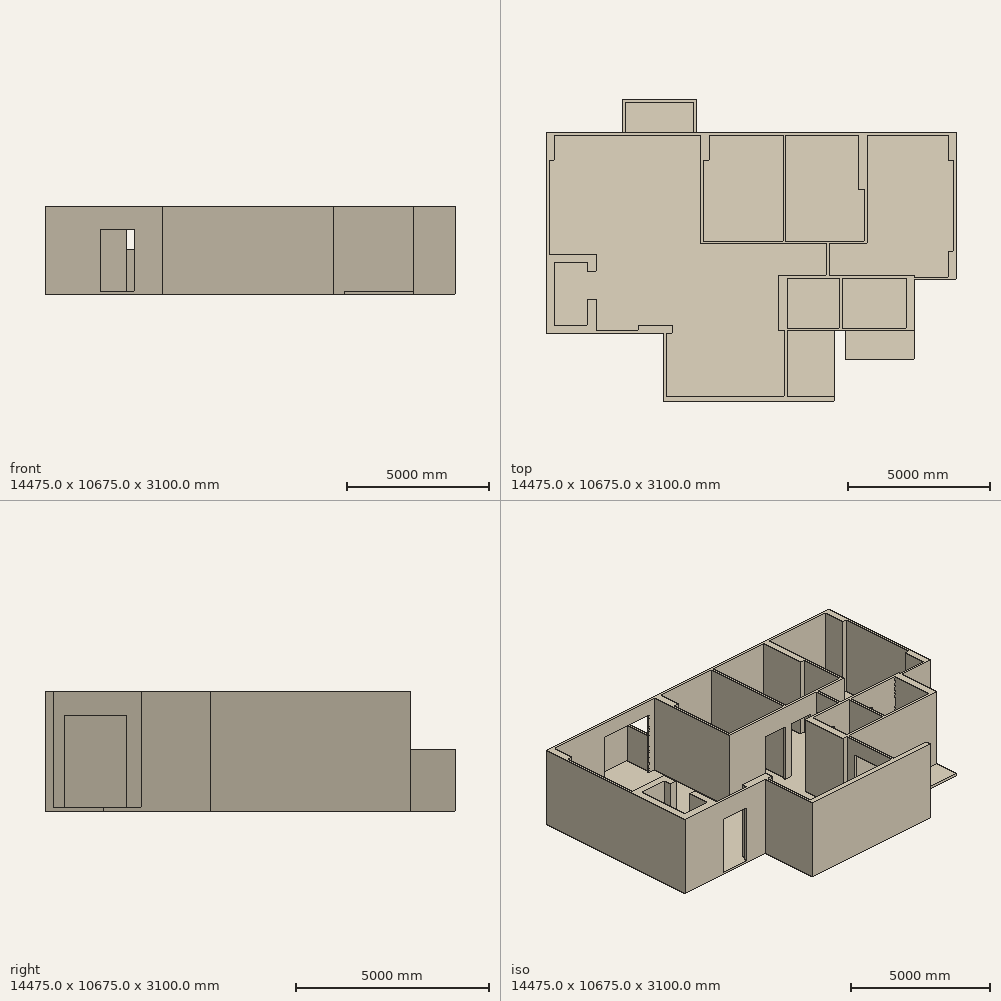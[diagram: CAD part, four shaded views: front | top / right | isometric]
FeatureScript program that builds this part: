
annotation { "Feature Type Name" : "Feature", "Feature Type Description" : "" }
export const myFeature = defineFeature(function(context is Context, id is Id, definition is map)
    precondition{}
    {
        {
            var Q0;
            Q0=qCreatedBy(makeId("Top.planeOp"),FACE);
            var sketch = newSketch(context, id + "F0", { "sketchPlane" : qUnion([Q0])});
            skLineSegment(sketch, "E0", {"start": v(0, 0) * mm, "end": v(-4125, 0) * mm});
            skLineSegment(sketch, "E1", {"start": v(-4125, 0) * mm, "end": v(-4125, 7100) * mm});
            skLineSegment(sketch, "E2", {"start": v(-4125, 7100) * mm, "end": v(-1425, 7100) * mm});
            skLineSegment(sketch, "E3", {"start": v(-1425, 7100) * mm, "end": v(-1425, 8275) * mm});
            skLineSegment(sketch, "E4", {"start": v(-1425, 8275) * mm, "end": v(1175, 8275) * mm});
            skLineSegment(sketch, "E5", {"start": v(1175, 8275) * mm, "end": v(1175, 7100) * mm});
            skLineSegment(sketch, "E6", {"start": v(1175, 7100) * mm, "end": v(10350, 7100) * mm});
            skLineSegment(sketch, "E7", {"start": v(10350, 7100) * mm, "end": v(10350, 1900) * mm});
            skLineSegment(sketch, "E8", {"start": v(10350, 1900) * mm, "end": v(8875, 1900) * mm});
            skLineSegment(sketch, "E9", {"start": v(8875, 1900) * mm, "end": v(8875, -900) * mm});
            skLineSegment(sketch, "E10", {"start": v(8875, -900) * mm, "end": v(6425, -900) * mm});
            skLineSegment(sketch, "E11", {"start": v(6050, -900) * mm, "end": v(6050, -2400) * mm});
            skLineSegment(sketch, "E12", {"start": v(6050, -2400) * mm, "end": v(0, -2400) * mm});
            skLineSegment(sketch, "E13", {"start": v(0, -2400) * mm, "end": v(0, 0) * mm});
            skLineSegment(sketch, "E14", {"start": v(6425, -900) * mm, "end": v(6425, 0) * mm});
            skLineSegment(sketch, "E15", {"start": v(6050, 0) * mm, "end": v(6050, -900) * mm});
            skLineSegment(sketch, "E16", {"start": v(6050, 0) * mm, "end": v(6050, 100) * mm});
            skLineSegment(sketch, "E17", {"start": v(6050, 100) * mm, "end": v(6425, 100) * mm});
            skLineSegment(sketch, "E18", {"start": v(6425, 100) * mm, "end": v(6425, 0) * mm});
            skSolve(sketch);
        }
        {
            var Q0;
            Q0=qSketchRegion(id+"F0",true);
            extrude(context, id + "F1", {"entities" : qUnion([Q0]), "oppositeDirection" : true, "depth" : 100 * mm});
        }
        {
            var Q0;
            Q0=makeQuery(id+"F1.opExtrude","CAP_FACE",FACE,{"disambiguationData":[OSD([sQuery(id+"F0.wireOp",EDGE,"E0"),sQuery(id+"F0.wireOp",EDGE,"E1"),sQuery(id+"F0.wireOp",EDGE,"E2"),sQuery(id+"F0.wireOp",EDGE,"E3"),sQuery(id+"F0.wireOp",EDGE,"E4"),sQuery(id+"F0.wireOp",EDGE,"E5"),sQuery(id+"F0.wireOp",EDGE,"E6"),sQuery(id+"F0.wireOp",EDGE,"E7"),sQuery(id+"F0.wireOp",EDGE,"E8"),sQuery(id+"F0.wireOp",EDGE,"E9"),sQuery(id+"F0.wireOp",EDGE,"E10"),sQuery(id+"F0.wireOp",EDGE,"E11"),sQuery(id+"F0.wireOp",EDGE,"E12"),sQuery(id+"F0.wireOp",EDGE,"E13"),sQuery(id+"F0.wireOp",EDGE,"E14"),sQuery(id+"F0.wireOp",EDGE,"EO6Hl1aY-iN83-L0no-XnAw-wlp1sX6jhs91"),sQuery(id+"F0.wireOp",EDGE,"E15")])],"isStart":true});
            var sketch = newSketch(context, id + "F2", { "sketchPlane" : qUnion([Q0])});
            skLineSegment(sketch, "E19", {"start": v(-4125, 0) * mm, "end": v(-4125, 2800) * mm});
            skLineSegment(sketch, "E20", {"start": v(-4125, 2800) * mm, "end": v(-2375, 2800) * mm});
            skLineSegment(sketch, "E21", {"start": v(-2375, 2800) * mm, "end": v(-2375, 2200) * mm});
            skLineSegment(sketch, "E22", {"start": v(-2375, 2200) * mm, "end": v(-2675, 2200) * mm});
            skLineSegment(sketch, "E23", {"start": v(-2675, 2200) * mm, "end": v(-2675, 2500) * mm});
            skLineSegment(sketch, "E24", {"start": v(-2675, 2500) * mm, "end": v(-3825, 2500) * mm});
            skLineSegment(sketch, "E25", {"start": v(-3825, 2500) * mm, "end": v(-3825, 300) * mm});
            skLineSegment(sketch, "E26", {"start": v(-3825, 300) * mm, "end": v(-2675, 300) * mm});
            skLineSegment(sketch, "E27", {"start": v(-2675, 300) * mm, "end": v(-2675, 1200) * mm});
            skLineSegment(sketch, "E28", {"start": v(-2675, 1200) * mm, "end": v(-2375, 1200) * mm});
            skLineSegment(sketch, "E29", {"start": v(-2375, 1200) * mm, "end": v(-2375, 0) * mm});
            skLineSegment(sketch, "E30", {"start": v(-2375, 0) * mm, "end": v(-4125, 0) * mm});
            skSolve(sketch);
        }
        {
            var Q0;
            Q0=qSketchRegion(id+"F2",true);
            extrude(context, id + "F3", {"entities" : qUnion([Q0]), "operationType" : NewBodyOperationType.ADD, "depth" : 3000 * mm});
        }
        {
            var Q0;
            Q0=makeQuery(id+"F1.opExtrude","CAP_FACE",FACE,{"disambiguationData":[OSD([sQuery(id+"F0.wireOp",EDGE,"E0"),sQuery(id+"F0.wireOp",EDGE,"E1"),sQuery(id+"F0.wireOp",EDGE,"E2"),sQuery(id+"F0.wireOp",EDGE,"E3"),sQuery(id+"F0.wireOp",EDGE,"E4"),sQuery(id+"F0.wireOp",EDGE,"E5"),sQuery(id+"F0.wireOp",EDGE,"E6"),sQuery(id+"F0.wireOp",EDGE,"E7"),sQuery(id+"F0.wireOp",EDGE,"E8"),sQuery(id+"F0.wireOp",EDGE,"E9"),sQuery(id+"F0.wireOp",EDGE,"E10"),sQuery(id+"F0.wireOp",EDGE,"E11"),sQuery(id+"F0.wireOp",EDGE,"E12"),sQuery(id+"F0.wireOp",EDGE,"E13"),sQuery(id+"F0.wireOp",EDGE,"E14"),sQuery(id+"F0.wireOp",EDGE,"EO6Hl1aY-iN83-L0no-XnAw-wlp1sX6jhs91"),sQuery(id+"F0.wireOp",EDGE,"E15")])],"isStart":true});
            var sketch = newSketch(context, id + "F4", { "sketchPlane" : qUnion([Q0])});
            skLineSegment(sketch, "E31.bottom", {"start": v(-4125, 7100) * mm, "end": v(-3825, 7100) * mm});
            skLineSegment(sketch, "E31.top", {"start": v(-4125, 6100) * mm, "end": v(-3825, 6100) * mm});
            skLineSegment(sketch, "E31.left", {"start": v(-4125, 7100) * mm, "end": v(-4125, 6100) * mm});
            skLineSegment(sketch, "E31.right", {"start": v(-3825, 7100) * mm, "end": v(-3825, 6100) * mm});
            skLineSegment(sketch, "E32.bottom", {"start": v(1325, 7100) * mm, "end": v(1625, 7100) * mm});
            skLineSegment(sketch, "E32.top", {"start": v(1325, 6100) * mm, "end": v(1625, 6100) * mm});
            skLineSegment(sketch, "E32.left", {"start": v(1325, 7100) * mm, "end": v(1325, 6100) * mm});
            skLineSegment(sketch, "E32.right", {"start": v(1625, 7100) * mm, "end": v(1625, 6100) * mm});
            skLineSegment(sketch, "E33.bottom", {"start": v(6900, 7100) * mm, "end": v(7200, 7100) * mm});
            skLineSegment(sketch, "E33.top", {"start": v(6900, 5100) * mm, "end": v(7200, 5100) * mm});
            skLineSegment(sketch, "E33.left", {"start": v(6900, 7100) * mm, "end": v(6900, 5100) * mm});
            skLineSegment(sketch, "E33.right", {"start": v(7200, 7100) * mm, "end": v(7200, 5100) * mm});
            skLineSegment(sketch, "E34.bottom", {"start": v(10350, 7100) * mm, "end": v(10050, 7100) * mm});
            skLineSegment(sketch, "E34.top", {"start": v(10350, 6100) * mm, "end": v(10050, 6100) * mm});
            skLineSegment(sketch, "E34.left", {"start": v(10350, 7100) * mm, "end": v(10350, 6100) * mm});
            skLineSegment(sketch, "E34.right", {"start": v(10050, 7100) * mm, "end": v(10050, 6100) * mm});
            skLineSegment(sketch, "E35.bottom", {"start": v(10350, 1900) * mm, "end": v(10050, 1900) * mm});
            skLineSegment(sketch, "E35.top", {"start": v(10350, 2900) * mm, "end": v(10050, 2900) * mm});
            skLineSegment(sketch, "E35.left", {"start": v(10350, 1900) * mm, "end": v(10350, 2900) * mm});
            skLineSegment(sketch, "E35.right", {"start": v(10050, 1900) * mm, "end": v(10050, 2900) * mm});
            skLineSegment(sketch, "E36.bottom", {"start": v(8875, 2050) * mm, "end": v(8575, 2050) * mm});
            skLineSegment(sketch, "E36.top", {"start": v(8875, 100) * mm, "end": v(8575, 100) * mm});
            skLineSegment(sketch, "E36.left", {"start": v(8875, 2050) * mm, "end": v(8875, 100) * mm});
            skLineSegment(sketch, "E36.right", {"start": v(8575, 2050) * mm, "end": v(8575, 100) * mm});
            skLineSegment(sketch, "E37.bottom", {"start": v(4375, 2050) * mm, "end": v(4075, 2050) * mm});
            skLineSegment(sketch, "E37.top", {"start": v(4375, 100) * mm, "end": v(4075, 100) * mm});
            skLineSegment(sketch, "E37.left", {"start": v(4375, 2050) * mm, "end": v(4375, 100) * mm});
            skLineSegment(sketch, "E37.right", {"start": v(4075, 2050) * mm, "end": v(4075, 100) * mm});
            skLineSegment(sketch, "E38.bottom", {"start": v(325, 0) * mm, "end": v(-875, 0) * mm});
            skLineSegment(sketch, "E38.top", {"start": v(325, 300) * mm, "end": v(-875, 300) * mm});
            skLineSegment(sketch, "E38.left", {"start": v(325, 0) * mm, "end": v(325, 300) * mm});
            skLineSegment(sketch, "E38.right", {"start": v(-875, 0) * mm, "end": v(-875, 300) * mm});
            skLineSegment(sketch, "E39.bottom", {"start": v(0, -2400) * mm, "end": v(6050, -2400) * mm});
            skLineSegment(sketch, "E39.top", {"start": v(0, -2200) * mm, "end": v(6050, -2200) * mm});
            skLineSegment(sketch, "E39.left", {"start": v(0, -2400) * mm, "end": v(0, -2200) * mm});
            skLineSegment(sketch, "E39.right", {"start": v(6050, -2400) * mm, "end": v(6050, -2200) * mm});
            skSolve(sketch);
        }
        {
            var Q0;
            Q0=qSketchRegion(id+"F4",true);
            extrude(context, id + "F5", {"entities" : qUnion([Q0]), "operationType" : NewBodyOperationType.ADD, "depth" : 3000 * mm});
        }
        {
            var Q0;
            Q0=makeQuery(id+"F1.opExtrude","CAP_FACE",FACE,{"disambiguationData":[OSD([sQuery(id+"F0.wireOp",EDGE,"E0"),sQuery(id+"F0.wireOp",EDGE,"E1"),sQuery(id+"F0.wireOp",EDGE,"E2"),sQuery(id+"F0.wireOp",EDGE,"E3"),sQuery(id+"F0.wireOp",EDGE,"E4"),sQuery(id+"F0.wireOp",EDGE,"E5"),sQuery(id+"F0.wireOp",EDGE,"E6"),sQuery(id+"F0.wireOp",EDGE,"E7"),sQuery(id+"F0.wireOp",EDGE,"E8"),sQuery(id+"F0.wireOp",EDGE,"E9"),sQuery(id+"F0.wireOp",EDGE,"E10"),sQuery(id+"F0.wireOp",EDGE,"E11"),sQuery(id+"F0.wireOp",EDGE,"E12"),sQuery(id+"F0.wireOp",EDGE,"E13"),sQuery(id+"F0.wireOp",EDGE,"E14"),sQuery(id+"F0.wireOp",EDGE,"EO6Hl1aY-iN83-L0no-XnAw-wlp1sX6jhs91"),sQuery(id+"F0.wireOp",EDGE,"E15")])],"isStart":true});
            var sketch = newSketch(context, id + "F6", { "sketchPlane" : qUnion([Q0])});
            skLineSegment(sketch, "E40", {"start": v(0, -2200) * mm, "end": v(0, 0) * mm});
            skLineSegment(sketch, "E41", {"start": v(0, 0) * mm, "end": v(-4125, 0) * mm});
            skLineSegment(sketch, "E42", {"start": v(-4125, 0) * mm, "end": v(-4125, 7100) * mm});
            skLineSegment(sketch, "E43", {"start": v(-4125, 7100) * mm, "end": v(-1425, 7100) * mm});
            skLineSegment(sketch, "E44", {"start": v(-1425, 7100) * mm, "end": v(-1425, 7000) * mm});
            skLineSegment(sketch, "E45", {"start": v(-1425, 7000) * mm, "end": v(-4025, 7000) * mm});
            skLineSegment(sketch, "E46", {"start": v(-4025, 7000) * mm, "end": v(-4025, 100) * mm});
            skLineSegment(sketch, "E47", {"start": v(-4025, 100) * mm, "end": v(100, 100) * mm});
            skLineSegment(sketch, "E48", {"start": v(100, 100) * mm, "end": v(100, -2200) * mm});
            skLineSegment(sketch, "E49", {"start": v(100, -2200) * mm, "end": v(0, -2200) * mm});
            skLineSegment(sketch, "E50.bottom", {"start": v(-1425, 7100) * mm, "end": v(1325, 7100) * mm});
            skLineSegment(sketch, "E50.top", {"start": v(-1425, 7000) * mm, "end": v(1325, 7000) * mm});
            skLineSegment(sketch, "E50.right", {"start": v(1325, 7100) * mm, "end": v(1325, 7000) * mm});
            skSolve(sketch);
        }
        {
            var Q0;
            Q0=qSketchRegion(id+"F6",true);
            extrude(context, id + "F7", {"entities" : qUnion([Q0]), "depth" : 3000 * mm});
        }
        {
            var Q0;
            Q0=makeQuery(id+"F1.opExtrude","CAP_FACE",FACE,{"disambiguationData":[OSD([sQuery(id+"F0.wireOp",EDGE,"E0"),sQuery(id+"F0.wireOp",EDGE,"E1"),sQuery(id+"F0.wireOp",EDGE,"E2"),sQuery(id+"F0.wireOp",EDGE,"E3"),sQuery(id+"F0.wireOp",EDGE,"E4"),sQuery(id+"F0.wireOp",EDGE,"E5"),sQuery(id+"F0.wireOp",EDGE,"E6"),sQuery(id+"F0.wireOp",EDGE,"E7"),sQuery(id+"F0.wireOp",EDGE,"E8"),sQuery(id+"F0.wireOp",EDGE,"E9"),sQuery(id+"F0.wireOp",EDGE,"E10"),sQuery(id+"F0.wireOp",EDGE,"E11"),sQuery(id+"F0.wireOp",EDGE,"E12"),sQuery(id+"F0.wireOp",EDGE,"E13"),sQuery(id+"F0.wireOp",EDGE,"E14"),sQuery(id+"F0.wireOp",EDGE,"EO6Hl1aY-iN83-L0no-XnAw-wlp1sX6jhs91"),sQuery(id+"F0.wireOp",EDGE,"E15")])],"isStart":true});
            var sketch = newSketch(context, id + "F8", { "sketchPlane" : qUnion([Q0])});
            skLineSegment(sketch, "E51", {"start": v(7200, 3170) * mm, "end": v(7200, 7100) * mm});
            skLineSegment(sketch, "E52", {"start": v(7200, 7100) * mm, "end": v(1325, 7100) * mm});
            skLineSegment(sketch, "E53", {"start": v(1325, 7100) * mm, "end": v(1325, 3170) * mm});
            skLineSegment(sketch, "E54", {"start": v(1325, 3170) * mm, "end": v(5775, 3170) * mm});
            skLineSegment(sketch, "E55.bottom", {"start": v(1425, 3270) * mm, "end": v(4225, 3270) * mm});
            skLineSegment(sketch, "E55.top", {"start": v(1425, 7000) * mm, "end": v(4225, 7000) * mm});
            skLineSegment(sketch, "E55.left", {"start": v(1425, 3270) * mm, "end": v(1425, 7000) * mm});
            skLineSegment(sketch, "E55.right", {"start": v(4225, 3270) * mm, "end": v(4225, 7000) * mm});
            skLineSegment(sketch, "E56.bottom", {"start": v(4325, 7000) * mm, "end": v(7100, 7000) * mm});
            skLineSegment(sketch, "E56.top", {"start": v(4325, 3270) * mm, "end": v(7100, 3270) * mm});
            skLineSegment(sketch, "E56.left", {"start": v(4325, 7000) * mm, "end": v(4325, 3270) * mm});
            skLineSegment(sketch, "E56.right", {"start": v(7100, 7000) * mm, "end": v(7100, 3270) * mm});
            skLineSegment(sketch, "E57.bottom", {"start": v(7200, 7100) * mm, "end": v(10350, 7100) * mm});
            skLineSegment(sketch, "E57.top", {"start": v(7200, 7000) * mm, "end": v(10250, 7000) * mm});
            skLineSegment(sketch, "E57.left", {"start": v(7200, 7100) * mm, "end": v(7200, 7000) * mm});
            skLineSegment(sketch, "E57.right", {"start": v(10350, 7100) * mm, "end": v(10350, 7000) * mm});
            skLineSegment(sketch, "E58.bottom", {"start": v(10350, 7100) * mm, "end": v(10250, 7100) * mm});
            skLineSegment(sketch, "E58.top", {"start": v(10350, 1900) * mm, "end": v(10250, 1900) * mm});
            skLineSegment(sketch, "E58.left", {"start": v(10350, 7100) * mm, "end": v(10350, 1900) * mm});
            skLineSegment(sketch, "E58.right", {"start": v(10250, 7000) * mm, "end": v(10250, 1975) * mm});
            skPoint(sketch, "E59.oppositeSnap0", {"position": v(8875, 1975) * mm});
            skLineSegment(sketch, "E59.bottom", {"start": v(10250, 1900) * mm, "end": v(8875, 1900) * mm});
            skLineSegment(sketch, "E59.top", {"start": v(10250, 1975) * mm, "end": v(8875, 1975) * mm});
            skLineSegment(sketch, "E59.right", {"start": v(8875, 1900) * mm, "end": v(8875, 1975) * mm});
            skLineSegment(sketch, "E60.bottom", {"start": v(8575, 2050) * mm, "end": v(5875, 2050) * mm});
            skLineSegment(sketch, "E60.top", {"start": v(8575, 1950) * mm, "end": v(6325, 1950) * mm});
            skLineSegment(sketch, "E60.left", {"start": v(8575, 2050) * mm, "end": v(8575, 1950) * mm});
            skLineSegment(sketch, "E60.right", {"start": v(4375, 2050) * mm, "end": v(4375, 1950) * mm});
            skLineSegment(sketch, "E61.bottom", {"start": v(4375, 100) * mm, "end": v(8575, 100) * mm});
            skLineSegment(sketch, "E61.top", {"start": v(4375, 200) * mm, "end": v(6225, 200) * mm});
            skLineSegment(sketch, "E61.left", {"start": v(4375, 100) * mm, "end": v(4375, 200) * mm});
            skLineSegment(sketch, "E61.right", {"start": v(8575, 100) * mm, "end": v(8575, 200) * mm});
            skLineSegment(sketch, "E62.left", {"start": v(6225, 1950) * mm, "end": v(6225, 200) * mm});
            skLineSegment(sketch, "E62.right", {"start": v(6325, 1950) * mm, "end": v(6325, 200) * mm});
            skLineSegment(sketch, "E63.trimOffspring", {"start": v(6225, 1950) * mm, "end": v(4375, 1950) * mm});
            skLineSegment(sketch, "E64.trimOffspring", {"start": v(6325, 200) * mm, "end": v(8575, 200) * mm});
            skLineSegment(sketch, "E65.left", {"start": v(5775, 3170) * mm, "end": v(5775, 2050) * mm});
            skLineSegment(sketch, "E65.right", {"start": v(5875, 3170) * mm, "end": v(5875, 2050) * mm});
            skLineSegment(sketch, "E66.trimOffspring", {"start": v(5875, 3170) * mm, "end": v(7200, 3170) * mm});
            skLineSegment(sketch, "E67.trimOffspring", {"start": v(5775, 2050) * mm, "end": v(4375, 2050) * mm});
            skLineSegment(sketch, "E68.bottom", {"start": v(4375, 200) * mm, "end": v(4275, 200) * mm});
            skLineSegment(sketch, "E68.top", {"start": v(4375, -2400) * mm, "end": v(4275, -2400) * mm});
            skLineSegment(sketch, "E68.left", {"start": v(4375, 200) * mm, "end": v(4375, -2400) * mm});
            skLineSegment(sketch, "E68.right", {"start": v(4275, 200) * mm, "end": v(4275, -2400) * mm});
            skSolve(sketch);
        }
        {
            var Q0;
            Q0=qSketchRegion(id+"F8",true);
            extrude(context, id + "F9", {"entities" : qUnion([Q0]), "operationType" : NewBodyOperationType.ADD, "depth" : 3000 * mm});
        }
        {
            var Q0;
            Q0=makeQuery(id+"F7.opExtrude","SWEPT_FACE",FACE,{"disambiguationData":[OSD([sQuery(id+"F6.wireOp",EDGE,"E41")])]});
            var sketch = newSketch(context, id + "F10", { "sketchPlane" : qUnion([Q0])});
            skLineSegment(sketch, "E69.bottom", {"start": v(-975, 0) * mm, "end": v(-2175, 0) * mm});
            skLineSegment(sketch, "E69.top", {"start": v(-975, 2200) * mm, "end": v(-2175, 2200) * mm});
            skLineSegment(sketch, "E69.left", {"start": v(-975, 0) * mm, "end": v(-975, 2200) * mm});
            skLineSegment(sketch, "E69.right", {"start": v(-2175, 0) * mm, "end": v(-2175, 2200) * mm});
            skSolve(sketch);
        }
        {
            var Q0;
            Q0=qSketchRegion(id+"F10",true);
            extrude(context, id + "F11", {"entities" : qUnion([Q0]), "operationType" : NewBodyOperationType.REMOVE, "oppositeDirection" : true, "depth" : 100 * mm});
        }
        {
            var Q0;
            Q0=makeQuery(id+"F9.opExtrude","SWEPT_FACE",FACE,{"disambiguationData":[OSD([sQuery(id+"F8.wireOp",EDGE,"E54")])]});
            var sketch = newSketch(context, id + "F12", { "sketchPlane" : qUnion([Q0])});
            skLineSegment(sketch, "E70.bottom", {"start": v(3175, 2200) * mm, "end": v(4175, 2200) * mm});
            skLineSegment(sketch, "E70.top", {"start": v(3175, 0) * mm, "end": v(4175, 0) * mm});
            skLineSegment(sketch, "E70.left", {"start": v(3175, 2200) * mm, "end": v(3175, 0) * mm});
            skLineSegment(sketch, "E70.right", {"start": v(4175, 2200) * mm, "end": v(4175, 0) * mm});
            skLineSegment(sketch, "E71.bottom", {"start": v(4475, 2200) * mm, "end": v(5475, 2200) * mm});
            skLineSegment(sketch, "E71.top", {"start": v(4475, 0) * mm, "end": v(5475, 0) * mm});
            skLineSegment(sketch, "E71.left", {"start": v(4475, 2200) * mm, "end": v(4475, 0) * mm});
            skLineSegment(sketch, "E71.right", {"start": v(5475, 2200) * mm, "end": v(5475, 0) * mm});
            skSolve(sketch);
        }
        {
            var Q0;
            Q0=qSketchRegion(id+"F12",true);
            extrude(context, id + "F13", {"entities" : qUnion([Q0]), "operationType" : NewBodyOperationType.REMOVE, "oppositeDirection" : true, "depth" : 100 * mm});
        }
        {
            var Q0;
            Q0=makeQuery(id+"F9.opExtrude","SWEPT_FACE",FACE,{"disambiguationData":[OSD([sQuery(id+"F8.wireOp",EDGE,"E65.left")])]});
            var sketch = newSketch(context, id + "F14", { "sketchPlane" : qUnion([Q0])});
            skLineSegment(sketch, "E72.bottom", {"start": v(-3110, 2200) * mm, "end": v(-2110, 2200) * mm});
            skLineSegment(sketch, "E72.top", {"start": v(-3110, 0) * mm, "end": v(-2110, 0) * mm});
            skLineSegment(sketch, "E72.left", {"start": v(-3110, 2200) * mm, "end": v(-3110, 0) * mm});
            skLineSegment(sketch, "E72.right", {"start": v(-2110, 2200) * mm, "end": v(-2110, 0) * mm});
            skSolve(sketch);
        }
        {
            var Q0;
            Q0=qSketchRegion(id+"F14",true);
            extrude(context, id + "F15", {"entities" : qUnion([Q0]), "operationType" : NewBodyOperationType.REMOVE, "oppositeDirection" : true, "depth" : 100 * mm});
        }
        {
            var Q0;
            Q0=makeQuery(id+"F9.opExtrude","SWEPT_FACE",FACE,{"disambiguationData":[OSD([sQuery(id+"F8.wireOp",EDGE,"E67.trimOffspring")])]});
            var sketch = newSketch(context, id + "F16", { "sketchPlane" : qUnion([Q0])});
            skLineSegment(sketch, "E73.bottom", {"start": v(-5475, 2200) * mm, "end": v(-4475, 2200) * mm});
            skLineSegment(sketch, "E73.top", {"start": v(-5475, 0) * mm, "end": v(-4475, 0) * mm});
            skLineSegment(sketch, "E73.left", {"start": v(-5475, 2200) * mm, "end": v(-5475, 0) * mm});
            skLineSegment(sketch, "E73.right", {"start": v(-4475, 2200) * mm, "end": v(-4475, 0) * mm});
            skPoint(sketch, "E74.oppositeSnap0", {"position": v(-5075, 0) * mm});
            skLineSegment(sketch, "E74.bottom", {"start": v(-6425, 2200) * mm, "end": v(-7425, 2200) * mm});
            skLineSegment(sketch, "E74.top", {"start": v(-6425, 0) * mm, "end": v(-7425, 0) * mm});
            skLineSegment(sketch, "E74.left", {"start": v(-6425, 2200) * mm, "end": v(-6425, 0) * mm});
            skLineSegment(sketch, "E74.right", {"start": v(-7425, 2200) * mm, "end": v(-7425, 0) * mm});
            skSolve(sketch);
        }
        {
            var Q0;
            Q0=qSketchRegion(id+"F16",true);
            extrude(context, id + "F17", {"entities" : qUnion([Q0]), "operationType" : NewBodyOperationType.REMOVE, "oppositeDirection" : true, "depth" : 100 * mm});
        }
        {
            var Q0;
            Q0=makeQuery(id+"F9.opExtrude","SWEPT_FACE",FACE,{"disambiguationData":[OSD([sQuery(id+"F8.wireOp",EDGE,"E68.right")])]});
            var sketch = newSketch(context, id + "F18", { "sketchPlane" : qUnion([Q0])});
            skLineSegment(sketch, "E75.bottom", {"start": v(300, 2400) * mm, "end": v(1900, 2400) * mm});
            skLineSegment(sketch, "E75.top", {"start": v(300, 0) * mm, "end": v(1900, 0) * mm});
            skLineSegment(sketch, "E75.left", {"start": v(300, 2400) * mm, "end": v(300, 0) * mm});
            skLineSegment(sketch, "E75.right", {"start": v(1900, 2400) * mm, "end": v(1900, 0) * mm});
            skSolve(sketch);
        }
        {
            var Q0;
            Q0=qSketchRegion(id+"F18",true);
            extrude(context, id + "F19", {"entities" : qUnion([Q0]), "operationType" : NewBodyOperationType.REMOVE, "oppositeDirection" : true, "depth" : 100 * mm});
        }
        {
            var Q0;
            Q0=makeQuery(id+"F7.opExtrude","SWEPT_FACE",FACE,{"disambiguationData":[OSD([sQuery(id+"F6.wireOp",EDGE,"E45"),sQuery(id+"F6.wireOp",EDGE,"E50.top")])]});
            var sketch = newSketch(context, id + "F20", { "sketchPlane" : qUnion([Q0])});
            skLineSegment(sketch, "E76.bottom", {"start": v(-1275, 2400) * mm, "end": v(1025, 2400) * mm});
            skLineSegment(sketch, "E76.top", {"start": v(-1275, 0) * mm, "end": v(1025, 0) * mm});
            skLineSegment(sketch, "E76.left", {"start": v(-1275, 2400) * mm, "end": v(-1275, 0) * mm});
            skLineSegment(sketch, "E76.right", {"start": v(1025, 2400) * mm, "end": v(1025, 0) * mm});
            skSolve(sketch);
        }
        {
            var Q0;
            Q0=qSketchRegion(id+"F20",true);
            extrude(context, id + "F21", {"entities" : qUnion([Q0]), "operationType" : NewBodyOperationType.REMOVE, "oppositeDirection" : true, "depth" : 100 * mm});
        }
        {
            var Q0;
            Q0=makeQuery(id+"F1.opExtrude","CAP_FACE",FACE,{"disambiguationData":[OSD([sQuery(id+"F0.wireOp",EDGE,"E0"),sQuery(id+"F0.wireOp",EDGE,"E1"),sQuery(id+"F0.wireOp",EDGE,"E2"),sQuery(id+"F0.wireOp",EDGE,"E3"),sQuery(id+"F0.wireOp",EDGE,"E4"),sQuery(id+"F0.wireOp",EDGE,"E5"),sQuery(id+"F0.wireOp",EDGE,"E6"),sQuery(id+"F0.wireOp",EDGE,"E7"),sQuery(id+"F0.wireOp",EDGE,"E8"),sQuery(id+"F0.wireOp",EDGE,"E9"),sQuery(id+"F0.wireOp",EDGE,"E10"),sQuery(id+"F0.wireOp",EDGE,"E11"),sQuery(id+"F0.wireOp",EDGE,"E12"),sQuery(id+"F0.wireOp",EDGE,"E13"),sQuery(id+"F0.wireOp",EDGE,"E14"),sQuery(id+"F0.wireOp",EDGE,"E15"),sQuery(id+"F0.wireOp",EDGE,"E16"),sQuery(id+"F0.wireOp",EDGE,"E17"),sQuery(id+"F0.wireOp",EDGE,"E18")])],"isStart":true});
            var sketch = newSketch(context, id + "F22", { "sketchPlane" : qUnion([Q0])});
            skLineSegment(sketch, "E77.bottom", {"start": v(6050, -2200) * mm, "end": v(5950, -2200) * mm});
            skLineSegment(sketch, "E77.top", {"start": v(6050, 100) * mm, "end": v(5950, 100) * mm});
            skLineSegment(sketch, "E77.left", {"start": v(6050, -2200) * mm, "end": v(6050, 100) * mm});
            skLineSegment(sketch, "E77.right", {"start": v(5950, -2200) * mm, "end": v(5950, 100) * mm});
            skLineSegment(sketch, "E78", {"start": v(-1425, 7100) * mm, "end": v(-1425, 8275) * mm});
            skLineSegment(sketch, "E79", {"start": v(-1425, 8275) * mm, "end": v(1175, 8275) * mm});
            skLineSegment(sketch, "E80", {"start": v(1175, 8275) * mm, "end": v(1175, 7100) * mm});
            skLineSegment(sketch, "E81", {"start": v(1175, 7100) * mm, "end": v(1075, 7100) * mm});
            skLineSegment(sketch, "E82", {"start": v(1075, 7100) * mm, "end": v(1075, 8175) * mm});
            skLineSegment(sketch, "E83", {"start": v(1075, 8175) * mm, "end": v(-1325, 8175) * mm});
            skLineSegment(sketch, "E84", {"start": v(-1325, 8175) * mm, "end": v(-1325, 7100) * mm});
            skLineSegment(sketch, "E85", {"start": v(-1325, 7100) * mm, "end": v(-1425, 7100) * mm});
            skSolve(sketch);
        }
        {
            var Q0;
            Q0=makeQuery(id+"F22.imprint","IMPRINT",FACE,{"disambiguationData":[TD([[makeQuery(id+"F22.imprint","IMPRINT",EDGE,{"derivedFrom":sQuery(id+"F22.wireOp",EDGE,"E78")}),-1.0]])]});
            var Q1;
            Q1=makeQuery(id+"F22.imprint","IMPRINT",FACE,{"disambiguationData":[TD([[makeQuery(id+"F22.imprint","IMPRINT",EDGE,{"derivedFrom":sQuery(id+"F22.wireOp",EDGE,"E77.bottom")}),1.0]])]});
            extrude(context, id + "F23", {"entities" : qUnion([Q0, Q1]), "operationType" : NewBodyOperationType.ADD, "depth" : 1500 * mm});
        }
    });
